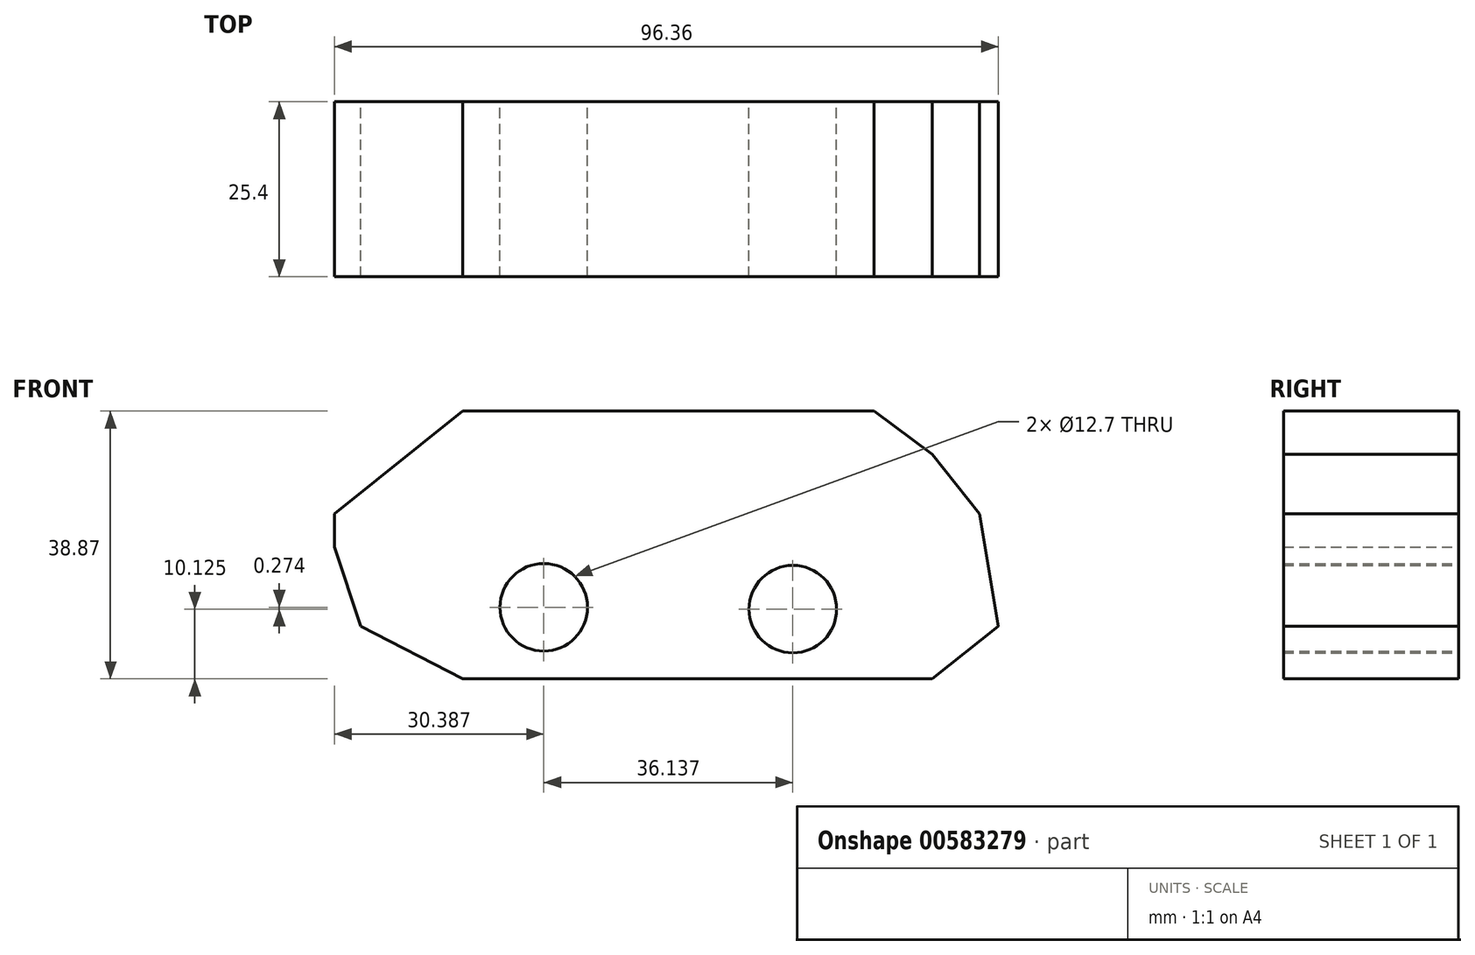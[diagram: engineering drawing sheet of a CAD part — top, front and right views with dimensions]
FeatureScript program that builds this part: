
annotation { "Feature Type Name" : "Feature", "Feature Type Description" : "" }
export const myFeature = defineFeature(function(context is Context, id is Id, definition is map)
    precondition{}
    {
        {
            var Q0;
            Q0=qCreatedBy(makeId("Front.planeOp"),FACE);
            var sketch = newSketch(context, id + "F0", { "sketchPlane" : qUnion([Q0])});
            skLineSegment(sketch, "E0", {"start": v(-30.53, 14.92) * mm, "end": v(29.16, 14.92) * mm});
            skLineSegment(sketch, "E1", {"start": v(29.16, 14.92) * mm, "end": v(37.64, 8.62) * mm});
            skLineSegment(sketch, "E2", {"start": v(37.64, 8.62) * mm, "end": v(44.49, 0) * mm});
            skLineSegment(sketch, "E3", {"start": v(44.49, 0) * mm, "end": v(47.22, -16.29) * mm});
            skLineSegment(sketch, "E4", {"start": v(47.22, -16.29) * mm, "end": v(37.64, -23.95) * mm});
            skLineSegment(sketch, "E5", {"start": v(37.64, -23.95) * mm, "end": v(-30.53, -23.95) * mm});
            skLineSegment(sketch, "E6", {"start": v(-30.53, -23.95) * mm, "end": v(-45.3, -16.29) * mm});
            skLineSegment(sketch, "E7", {"start": v(-45.3, -16.29) * mm, "end": v(-49.14, -4.8) * mm});
            skLineSegment(sketch, "E8", {"start": v(-49.14, -4.8) * mm, "end": v(-49.14, 0) * mm});
            skLineSegment(sketch, "E9", {"start": v(-49.14, 0) * mm, "end": v(-30.53, 14.92) * mm});
            skCircle(sketch, "E10", {"center": v(-18.75, -13.55) * mm, "radius": 6.35 * mm});
            skCircle(sketch, "E11", {"center": v(17.38, -13.83) * mm, "radius": 6.35 * mm});
            skSolve(sketch);
        }
        {
            var Q0;
            Q0=makeQuery(id+"F0.imprint","IMPRINT",FACE,{"disambiguationData":[TD([[makeQuery(id+"F0.imprint","IMPRINT",EDGE,{"derivedFrom":sQuery(id+"F0.wireOp",EDGE,"E0")}),-1.0]])]});
            extrude(context, id + "F1", {"entities" : qUnion([Q0]), "depth" : 25.4 * mm, "offsetDistance" : 25.4 * mm});
        }
    });
